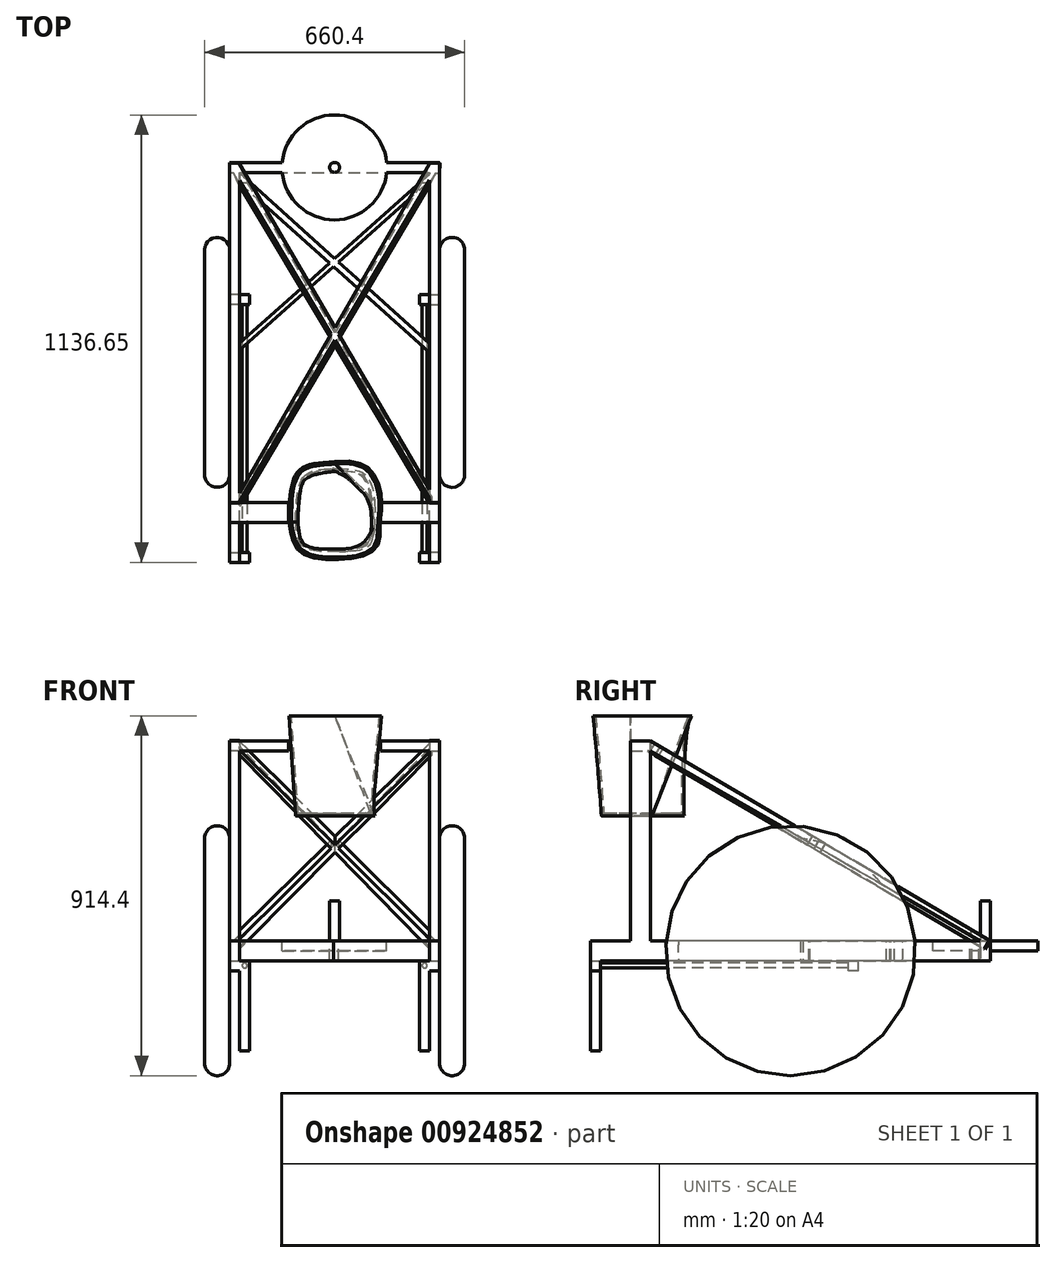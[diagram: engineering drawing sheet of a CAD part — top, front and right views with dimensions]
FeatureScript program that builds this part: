
annotation { "Feature Type Name" : "Feature", "Feature Type Description" : "" }
export const myFeature = defineFeature(function(context is Context, id is Id, definition is map)
    precondition{}
    {
        {
            var Q0;
            Q0=qCreatedBy(makeId("Right.planeOp"),FACE);
            var sketch = newSketch(context, id + "F0", { "sketchPlane" : qUnion([Q0])});
            skCircle(sketch, "E0", {"center": v(0, 317.5) * mm, "radius": 317.5 * mm});
            skSolve(sketch);
        }
        {
            var Q0;
            Q0=makeQuery(id+"F0.imprint","IMPRINT",FACE,{"disambiguationData":[TD([[makeQuery(id+"F0.imprint","IMPRINT",EDGE,{"derivedFrom":sQuery(id+"F0.wireOp",EDGE,"E0")}),1.0]])]});
            extrude(context, id + "F1", {"entities" : qUnion([Q0]), "depth" : 330.2 * mm, "offsetDistance" : 25.4 * mm, "hasSecondDirection" : true, "secondDirectionOppositeDirection" : false, "secondDirectionDepth" : 266.7 * mm});
        }
        {
            var Q0;
            Q0=makeQuery(id+"FX83OG7cxAnBelo_1.opExtrude","CAP_EDGE",EDGE,{"disambiguationData":[OSD([sQuery(id+"F0.wireOp",EDGE,"E0")])],"isStart":false});
            var Q1;
            Q1=makeQuery(id+"FX83OG7cxAnBelo_1.opExtrude","CAP_EDGE",EDGE,{"disambiguationData":[OSD([sQuery(id+"F0.wireOp",EDGE,"E0")])],"isStart":true});
            var Q2;
            Q2=makeQuery(id+"F1.opExtrude","CAP_EDGE",EDGE,{"disambiguationData":[OSD([sQuery(id+"F0.wireOp",EDGE,"E0")])],"isStart":true});
            var Q3;
            Q3=makeQuery(id+"F1.opExtrude","SWEPT_FACE",FACE,{"disambiguationData":[OSD([sQuery(id+"F0.wireOp",EDGE,"E0")])]});
            fillet(context, id + "F2", {"entities" : qUnion([Q0, Q1, Q2, Q3]), "radius" : 31.75 * mm, "tangentPropagation" : true, "allowEdgeOverflow" : false});
        }
        {
            var Q0;
            Q0=qCreatedBy(makeId("Top.planeOp"),FACE);
            cPlane(context, id + "F3", {"entities" : qUnion([Q0]), "cplaneType" : CPlaneType.OFFSET, "offset" : 317.5 * mm, "width" : 152.4 * mm, "height" : 152.4 * mm});
        }
        {
            var Q0;
            Q0=qCreatedBy(id+"F3.planeOp",FACE);
            var sketch = newSketch(context, id + "F4", { "sketchPlane" : qUnion([Q0])});
            skLineSegment(sketch, "E1.bottom", {"start": v(266.7, 508) * mm, "end": v(241.3, 508) * mm});
            skLineSegment(sketch, "E1.top", {"start": v(266.7, -508) * mm, "end": v(241.3, -508) * mm});
            skLineSegment(sketch, "E1.left", {"start": v(266.7, 508) * mm, "end": v(266.7, -508) * mm});
            skLineSegment(sketch, "E1.right", {"start": v(241.3, 508) * mm, "end": v(241.3, -508) * mm});
            skSolve(sketch);
        }
        {
            var Q0;
            Q0=makeQuery(id+"F4.imprint","IMPRINT",FACE,{"disambiguationData":[TD([[makeQuery(id+"F4.imprint","IMPRINT",EDGE,{"derivedFrom":sQuery(id+"F4.wireOp",EDGE,"E1.bottom")}),1.0]])]});
            extrude(context, id + "F5", {"entities" : qUnion([Q0]), "operationType" : NewBodyOperationType.ADD, "depth" : 25.4 * mm, "offsetDistance" : 25.4 * mm, "hasSecondDirection" : true, "secondDirectionOppositeDirection" : true, "secondDirectionDepth" : 25.4 * mm});
        }
        {
            var Q0;
            Q0=makeQuery(id+"F5.opExtrude","CAP_FACE",FACE,{"disambiguationData":[OSD([sQuery(id+"F4.wireOp",EDGE,"E1.bottom"),sQuery(id+"F4.wireOp",EDGE,"E1.top"),sQuery(id+"F4.wireOp",EDGE,"E1.left"),sQuery(id+"F4.wireOp",EDGE,"E1.right")])],"isStart":false});
            var sketch = newSketch(context, id + "F6", { "sketchPlane" : qUnion([Q0])});
            skLineSegment(sketch, "E2.bottom", {"start": v(266.7, -406.4) * mm, "end": v(241.3, -406.4) * mm});
            skLineSegment(sketch, "E2.top", {"start": v(266.7, -355.6) * mm, "end": v(241.3, -355.6) * mm});
            skLineSegment(sketch, "E2.left", {"start": v(266.7, -406.4) * mm, "end": v(266.7, -355.6) * mm});
            skLineSegment(sketch, "E2.right", {"start": v(241.3, -406.4) * mm, "end": v(241.3, -355.6) * mm});
            skSolve(sketch);
        }
        {
            var Q0;
            Q0=qSketchRegion(id+"F6",true);
            extrude(context, id + "F7", {"entities" : qUnion([Q0]), "operationType" : NewBodyOperationType.ADD, "depth" : 508 * mm, "offsetDistance" : 25.4 * mm});
        }
        {
            var Q0;
            Q0=makeQuery(id+"F5.opExtrude","CAP_FACE",FACE,{"disambiguationData":[OSD([sQuery(id+"F4.wireOp",EDGE,"E1.bottom"),sQuery(id+"F4.wireOp",EDGE,"E1.top"),sQuery(id+"F4.wireOp",EDGE,"E1.left"),sQuery(id+"F4.wireOp",EDGE,"E1.right")])],"isStart":true});
            var sketch = newSketch(context, id + "F8", { "sketchPlane" : qUnion([Q0])});
            skLineSegment(sketch, "E3.bottom", {"start": v(266.7, 508) * mm, "end": v(241.3, 508) * mm});
            skLineSegment(sketch, "E3.top", {"start": v(266.7, 482.6) * mm, "end": v(241.3, 482.6) * mm});
            skLineSegment(sketch, "E3.left", {"start": v(266.7, 508) * mm, "end": v(266.7, 482.6) * mm});
            skLineSegment(sketch, "E3.right", {"start": v(241.3, 508) * mm, "end": v(241.3, 482.6) * mm});
            skLineSegment(sketch, "E4.bottom", {"start": v(241.3, -172.43) * mm, "end": v(266.7, -172.43) * mm});
            skLineSegment(sketch, "E4.top", {"start": v(241.3, -147.03) * mm, "end": v(266.7, -147.03) * mm});
            skLineSegment(sketch, "E4.left", {"start": v(241.3, -172.43) * mm, "end": v(241.3, -147.03) * mm});
            skLineSegment(sketch, "E4.right", {"start": v(266.7, -172.43) * mm, "end": v(266.7, -147.03) * mm});
            skSolve(sketch);
        }
        {
            var Q0;
            Q0=qSketchRegion(id+"F8",true);
            extrude(context, id + "F9", {"entities" : qUnion([Q0]), "operationType" : NewBodyOperationType.ADD, "depth" : 25.4 * mm, "offsetDistance" : 25.4 * mm});
        }
        {
            var Q0;
            Q0=makeQuery(id+"F9.boolean.opBoolean","MERGE",FACE,{"derivedFrom":[makeQuery(id+"F7.boolean.opBoolean","MERGE",FACE,{"derivedFrom":[makeQuery(id+"F5.opExtrude","SWEPT_FACE",FACE,{"disambiguationData":[OSD([sQuery(id+"F4.wireOp",EDGE,"E1.right")])]}),makeQuery(id+"F7.opExtrude","SWEPT_FACE",FACE,{"disambiguationData":[OSD([sQuery(id+"F6.wireOp",EDGE,"E2.right")])]})]}),makeQuery(id+"F9.opExtrude","SWEPT_FACE",FACE,{"disambiguationData":[OSD([sQuery(id+"F8.wireOp",EDGE,"E3.right")])]}),makeQuery(id+"F9.opExtrude","SWEPT_FACE",FACE,{"disambiguationData":[OSD([sQuery(id+"F8.wireOp",EDGE,"2GlEI7fU-vQDi-rjw4-ohAJ-rqm9R4m0vmAV.right")])]})]});
            var sketch = newSketch(context, id + "F10", { "sketchPlane" : qUnion([Q0])});
            skLineSegment(sketch, "E5.bottom", {"start": v(508, 266.7) * mm, "end": v(482.6, 266.7) * mm});
            skLineSegment(sketch, "E5.top", {"start": v(508, 292.1) * mm, "end": v(482.6, 292.1) * mm});
            skLineSegment(sketch, "E5.left", {"start": v(508, 266.7) * mm, "end": v(508, 292.1) * mm});
            skLineSegment(sketch, "E5.right", {"start": v(482.6, 266.7) * mm, "end": v(482.6, 292.1) * mm});
            skLineSegment(sketch, "E6.bottom", {"start": v(-172.43, 266.7) * mm, "end": v(-147.03, 266.7) * mm});
            skLineSegment(sketch, "E6.top", {"start": v(-172.43, 292.1) * mm, "end": v(-147.03, 292.1) * mm});
            skLineSegment(sketch, "E6.left", {"start": v(-172.43, 266.7) * mm, "end": v(-172.43, 292.1) * mm});
            skLineSegment(sketch, "E6.right", {"start": v(-147.03, 266.7) * mm, "end": v(-147.03, 292.1) * mm});
            skSolve(sketch);
        }
        {
            var Q0;
            Q0=qSketchRegion(id+"F10",true);
            extrude(context, id + "F11", {"entities" : qUnion([Q0]), "operationType" : NewBodyOperationType.ADD, "depth" : 25.4 * mm, "offsetDistance" : 25.4 * mm});
        }
        {
            var Q0;
            Q0=makeQuery(id+"F11.boolean.opBoolean","MERGE",FACE,{"derivedFrom":[makeQuery(id+"F9.opExtrude","SWEPT_FACE",FACE,{"disambiguationData":[OSD([sQuery(id+"F8.wireOp",EDGE,"E3.top")])]}),makeQuery(id+"F11.opExtrude","SWEPT_FACE",FACE,{"disambiguationData":[OSD([sQuery(id+"F10.wireOp",EDGE,"E5.right")])]})]});
            var sketch = newSketch(context, id + "F12", { "sketchPlane" : qUnion([Q0])});
            skCircle(sketch, "E7", {"center": v(-228.6, 279.75) * mm, "radius": 6.35 * mm});
            skSolve(sketch);
        }
        {
            var Q0;
            Q0=qSketchRegion(id+"F12",true);
            extrude(context, id + "F13", {"entities" : qUnion([Q0]), "operationType" : NewBodyOperationType.ADD, "depth" : 635 * mm, "offsetDistance" : 25.4 * mm});
        }
        {
            var Q0;
            Q0=makeQuery(id+"F9.boolean.opBoolean","MERGE",FACE,{"derivedFrom":[makeQuery(id+"F7.boolean.opBoolean","MERGE",FACE,{"derivedFrom":[makeQuery(id+"F5.opExtrude","SWEPT_FACE",FACE,{"disambiguationData":[OSD([sQuery(id+"F4.wireOp",EDGE,"E1.right")])]}),makeQuery(id+"F7.opExtrude","SWEPT_FACE",FACE,{"disambiguationData":[OSD([sQuery(id+"F6.wireOp",EDGE,"E2.right")])]})]}),makeQuery(id+"F9.opExtrude","SWEPT_FACE",FACE,{"disambiguationData":[OSD([sQuery(id+"F8.wireOp",EDGE,"E3.right")])]}),makeQuery(id+"F9.opExtrude","SWEPT_FACE",FACE,{"disambiguationData":[OSD([sQuery(id+"F8.wireOp",EDGE,"2GlEI7fU-vQDi-rjw4-ohAJ-rqm9R4m0vmAV.right")])]})]});
            var sketch = newSketch(context, id + "F14", { "sketchPlane" : qUnion([Q0])});
            skLineSegment(sketch, "E8.bottom", {"start": v(406.4, 850.9) * mm, "end": v(355.6, 850.9) * mm});
            skLineSegment(sketch, "E8.top", {"start": v(406.4, 825.5) * mm, "end": v(355.6, 825.5) * mm});
            skLineSegment(sketch, "E8.left", {"start": v(406.4, 850.9) * mm, "end": v(406.4, 825.5) * mm});
            skLineSegment(sketch, "E8.right", {"start": v(355.6, 850.9) * mm, "end": v(355.6, 825.5) * mm});
            skSolve(sketch);
        }
        {
            var Q0;
            Q0=qSketchRegion(id+"F14",true);
            extrude(context, id + "F15", {"entities" : qUnion([Q0]), "operationType" : NewBodyOperationType.ADD, "depth" : 124.28 * mm, "offsetDistance" : 25.4 * mm});
        }
        {
            var Q0;
            {var subQ0=sQuery(id+"F0.wireOp",EDGE,"E0");var subQ1=sQuery(id+"F4.wireOp",EDGE,"E1.left");Q0=makeQuery(id+"F5.boolean.opBoolean","SPLIT",FACE,{"disambiguationData":[TD([makeQuery(id+"F5.opExtrude","CAP_FACE",FACE,{"disambiguationData":[OSD([sQuery(id+"F4.wireOp",EDGE,"E1.bottom"),sQuery(id+"F4.wireOp",EDGE,"E1.top"),subQ1,sQuery(id+"F4.wireOp",EDGE,"E1.right")])],"isStart":false})])],"derivedFrom":makeQuery(id+"F1.opExtrude","CAP_FACE",FACE,{"disambiguationData":[OSD([subQ0])],"isStart":true})});}
            cPlane(context, id + "F16", {"entities" : qUnion([Q0]), "cplaneType" : CPlaneType.OFFSET, "offset" : 0 * mm, "width" : 152.4 * mm, "height" : 152.4 * mm});
        }
        {
            var Q0;
            Q0=qCreatedBy(id+"F16.planeOp",FACE);
            var sketch = newSketch(context, id + "F17", { "sketchPlane" : qUnion([Q0])});
            skLineSegment(sketch, "E9", {"start": v(-507.39, 342.38) * mm, "end": v(356.93, 851.2) * mm});
            skLineSegment(sketch, "E10", {"start": v(356.93, 851.2) * mm, "end": v(356.93, 825.8) * mm});
            skLineSegment(sketch, "E11", {"start": v(356.93, 825.8) * mm, "end": v(-481.99, 342.38) * mm});
            skLineSegment(sketch, "E12", {"start": v(-481.99, 342.38) * mm, "end": v(-507.39, 342.38) * mm});
            skSolve(sketch);
        }
        {
            var Q0;
            Q0=qSketchRegion(id+"F17",true);
            extrude(context, id + "F18", {"entities" : qUnion([Q0]), "operationType" : NewBodyOperationType.ADD, "depth" : 25.4 * mm, "offsetDistance" : 25.4 * mm});
        }
        {
            var Q0;
            Q0=makeQuery(id+"F1.opExtrude","SWEPT_BODY",BODY,{"disambiguationData":[OSD([sQuery(id+"F0.wireOp",EDGE,"E0")])]});
            var Q1;
            Q1=qCreatedBy(makeId("Right.planeOp"),FACE);
            mirror(context, id + "F19", {"operationType" : NewBodyOperationType.ADD, "entities" : qUnion([Q0]), "mirrorPlane" : qUnion([Q1])});
        }
        {
            var Q0;
            {var subQ0=sQuery(id+"F0.wireOp",EDGE,"E0");var subQ6=sQuery(id+"F17.wireOp",EDGE,"E9");Q0=makeQuery(id+"F18.boolean.opBoolean","SPLIT",FACE,{"disambiguationData":[TD([makeQuery(id+"F1.opExtrude","CAP_FACE",FACE,{"disambiguationData":[OSD([subQ0])],"isStart":true})])],"derivedFrom":makeQuery(id+"F18.opExtrude","SWEPT_FACE",FACE,{"disambiguationData":[OSD([subQ6])]})});}
            cPlane(context, id + "F20", {"entities" : qUnion([Q0]), "cplaneType" : CPlaneType.OFFSET, "offset" : 0 * mm, "oppositeDirection" : true, "width" : 152.4 * mm, "height" : 152.4 * mm});
        }
        {
            var Q0;
            Q0=qCreatedBy(id+"F20.planeOp",FACE);
            var sketch = newSketch(context, id + "F21", { "sketchPlane" : qUnion([Q0])});
            skLineSegment(sketch, "E13", {"start": v(-267.5, 260.99) * mm, "end": v(245.57, -734.84) * mm});
            skLineSegment(sketch, "E14", {"start": v(245.57, -734.84) * mm, "end": v(245.57, -709.44) * mm});
            skLineSegment(sketch, "E15", {"start": v(245.57, -709.44) * mm, "end": v(-242.1, 260.98) * mm});
            skLineSegment(sketch, "E16", {"start": v(-242.1, 260.98) * mm, "end": v(-267.5, 260.99) * mm});
            skSolve(sketch);
        }
        {
            var Q0;
            Q0=qSketchRegion(id+"F21",true);
            extrude(context, id + "F22", {"entities" : qUnion([Q0]), "operationType" : NewBodyOperationType.ADD, "oppositeDirection" : true, "depth" : 25.4 * mm, "offsetDistance" : 25.4 * mm});
        }
        {
            var Q0;
            Q0=qCreatedBy(id+"F20.planeOp",FACE);
            var sketch = newSketch(context, id + "F23", { "sketchPlane" : qUnion([Q0])});
            skLineSegment(sketch, "E17", {"start": v(-242.02, -737.2) * mm, "end": v(267.33, 262.61) * mm});
            skLineSegment(sketch, "E18", {"start": v(267.33, 262.61) * mm, "end": v(241.93, 262.61) * mm});
            skLineSegment(sketch, "E19", {"start": v(-242.02, -737.2) * mm, "end": v(-242.02, -711.8) * mm});
            skLineSegment(sketch, "E20", {"start": v(241.93, 262.61) * mm, "end": v(-242.02, -711.8) * mm});
            skSolve(sketch);
        }
        {
            var Q0;
            Q0=qSketchRegion(id+"F23",true);
            extrude(context, id + "F24", {"entities" : qUnion([Q0]), "operationType" : NewBodyOperationType.ADD, "oppositeDirection" : true, "depth" : 25.4 * mm, "offsetDistance" : 25.4 * mm});
        }
        {
            var Q0;
            {var subQ0=sQuery(id+"F17.wireOp",EDGE,"E11");var subQ1=sQuery(id+"F17.wireOp",EDGE,"E9");var subQ6=sQuery(id+"F4.wireOp",EDGE,"E1.right");var subQ9=sQuery(id+"F4.wireOp",EDGE,"E1.bottom");var subQ10=sQuery(id+"F17.wireOp",EDGE,"E12");Q0=makeQuery(id+"F22.boolean.opBoolean","SPLIT",FACE,{"disambiguationData":[TD([makeQuery(id+"F5.opExtrude","SWEPT_FACE",FACE,{"disambiguationData":[OSD([subQ9])]})])],"derivedFrom":makeQuery(id+"F18.boolean.opBoolean","MERGE",FACE,{"derivedFrom":[makeQuery(id+"F9.boolean.opBoolean","MERGE",FACE,{"derivedFrom":[makeQuery(id+"F7.boolean.opBoolean","MERGE",FACE,{"derivedFrom":[makeQuery(id+"F5.opExtrude","SWEPT_FACE",FACE,{"disambiguationData":[OSD([subQ6])]}),makeQuery(id+"F7.opExtrude","SWEPT_FACE",FACE,{"disambiguationData":[OSD([sQuery(id+"F6.wireOp",EDGE,"E2.right")])]})]}),makeQuery(id+"F9.opExtrude","SWEPT_FACE",FACE,{"disambiguationData":[OSD([sQuery(id+"F8.wireOp",EDGE,"E3.right")])]}),makeQuery(id+"F9.opExtrude","SWEPT_FACE",FACE,{"disambiguationData":[OSD([sQuery(id+"F8.wireOp",EDGE,"E4.left")])]})]}),makeQuery(id+"F18.opExtrude","CAP_FACE",FACE,{"disambiguationData":[OSD([subQ1,sQuery(id+"F17.wireOp",EDGE,"E10"),subQ0,subQ10])],"isStart":false})]})});}
            var sketch = newSketch(context, id + "F25", { "sketchPlane" : qUnion([Q0])});
            skLineSegment(sketch, "E21.bottom", {"start": v(-508, 342.9) * mm, "end": v(-482.6, 342.9) * mm});
            skLineSegment(sketch, "E21.top", {"start": v(-508, 292.1) * mm, "end": v(-482.6, 292.1) * mm});
            skLineSegment(sketch, "E21.left", {"start": v(-508, 342.9) * mm, "end": v(-508, 292.1) * mm});
            skLineSegment(sketch, "E21.right", {"start": v(-482.6, 342.9) * mm, "end": v(-482.6, 292.1) * mm});
            skSolve(sketch);
        }
        {
            var Q0;
            Q0=qSketchRegion(id+"F25",true);
            extrude(context, id + "F26", {"entities" : qUnion([Q0]), "operationType" : NewBodyOperationType.ADD, "depth" : 482.6 * mm, "offsetDistance" : 25.4 * mm});
        }
        {
            var Q0;
            {var subQ0=sQuery(id+"F4.wireOp",EDGE,"E1.left");var subQ2=sQuery(id+"F4.wireOp",EDGE,"E1.bottom");var subQ3=makeQuery(id+"F5.opExtrude","SWEPT_FACE",FACE,{"disambiguationData":[OSD([subQ2])]});var subQ4=sQuery(id+"F0.wireOp",EDGE,"E0");var subQ6=makeQuery(id+"F1.opExtrude","CAP_FACE",FACE,{"disambiguationData":[OSD([subQ4])],"isStart":true});var subQ8=sQuery(id+"F4.wireOp",EDGE,"E1.right");var subQ11=makeQuery(id+"F18.boolean.opBoolean","SPLIT",FACE,{"disambiguationData":[TD([subQ3])],"derivedFrom":makeQuery(id+"F7.boolean.opBoolean","SPLIT",FACE,{"disambiguationData":[TD([subQ6])],"derivedFrom":makeQuery(id+"F5.opExtrude","CAP_FACE",FACE,{"disambiguationData":[OSD([subQ2,sQuery(id+"F4.wireOp",EDGE,"E1.top"),subQ0,subQ8])],"isStart":false})})});Q0=makeQuery(id+"F26.boolean.opBoolean","MERGE",FACE,{"derivedFrom":[makeQuery(id+"F19.opPattern","COPY",FACE,{"derivedFrom":subQ11,"instanceName":"1"}),subQ11,makeQuery(id+"F26.opExtrude","SWEPT_FACE",FACE,{"disambiguationData":[OSD([sQuery(id+"F25.wireOp",EDGE,"E21.bottom")])]})]});}
            var sketch = newSketch(context, id + "F27", { "sketchPlane" : qUnion([Q0])});
            skCircle(sketch, "E22", {"center": v(-0.43, 495.3) * mm, "radius": 133.35 * mm});
            skPoint(sketch, "E22.centerSnap0", {"position": v(-0.43, 482.6) * mm});
            skSolve(sketch);
        }
        {
            var Q0;
            {var subQ0=sQuery(id+"F27.wireOp",EDGE,"E22");var subQ1=makeQuery(id+"F26.opExtrude","SWEPT_EDGE",EDGE,{"disambiguationData":[OSD([sQuery(id+"F4.wireOp",EDGE,"E1.right"),sQuery(id+"F25.wireOp",EDGE,"E21.bottom"),sQuery(id+"F25.wireOp",EDGE,"E21.right")])]});var subQ2=makeQuery(id+"F27.imprint","INTERSECT",VERTEX,{"disambiguationData":[OD(0.0)],"derivedFrom":[subQ1,subQ0]});Q0=makeQuery(id+"F27.imprint","IMPRINT",FACE,{"disambiguationData":[TD([[makeQuery(id+"F27.imprint","IMPRINT",EDGE,{"disambiguationData":[TD([[subQ2,-1.0]])],"derivedFrom":subQ0}),1.0]])]});}
            var Q1;
            {var subQ0=sQuery(id+"F27.wireOp",EDGE,"E22");var subQ1=sQuery(id+"F25.wireOp",EDGE,"E21.bottom");var subQ5=makeQuery(id+"F26.opExtrude","SWEPT_EDGE",EDGE,{"disambiguationData":[OSD([sQuery(id+"F4.wireOp",EDGE,"E1.right"),subQ1,sQuery(id+"F25.wireOp",EDGE,"E21.right")])]});var subQ6=makeQuery(id+"F27.imprint","INTERSECT",VERTEX,{"disambiguationData":[OD(0.0)],"derivedFrom":[subQ5,subQ0]});Q1=makeQuery(id+"F27.imprint","IMPRINT",FACE,{"disambiguationData":[TD([[makeQuery(id+"F27.imprint","IMPRINT",EDGE,{"disambiguationData":[TD([[subQ6,1.0]])],"derivedFrom":subQ0}),1.0]])]});}
            var Q2;
            {var subQ0=sQuery(id+"F27.wireOp",EDGE,"E22");var subQ1=makeQuery(id+"F5.opExtrude","CAP_EDGE",EDGE,{"disambiguationData":[OSD([sQuery(id+"F4.wireOp",EDGE,"E1.bottom")])],"isStart":false});var subQ2=makeQuery(id+"F26.boolean.opBoolean","MERGE",EDGE,{"derivedFrom":[subQ1,makeQuery(id+"F19.opPattern","COPY",EDGE,{"derivedFrom":subQ1,"instanceName":"1"}),makeQuery(id+"F26.opExtrude","SWEPT_EDGE",EDGE,{"disambiguationData":[OSD([sQuery(id+"F25.wireOp",EDGE,"E21.bottom"),sQuery(id+"F25.wireOp",EDGE,"E21.left")])]})]});var subQ3=makeQuery(id+"F27.imprint","INTERSECT",VERTEX,{"disambiguationData":[OD(0.0)],"derivedFrom":[subQ2,subQ0]});Q2=makeQuery(id+"F27.imprint","IMPRINT",FACE,{"disambiguationData":[TD([[makeQuery(id+"F27.imprint","IMPRINT",EDGE,{"disambiguationData":[TD([[subQ3,1.0]])],"derivedFrom":subQ0}),1.0]])]});}
            extrude(context, id + "F28", {"entities" : qUnion([Q0, Q1, Q2]), "operationType" : NewBodyOperationType.ADD, "oppositeDirection" : true, "depth" : 25.4 * mm, "offsetDistance" : 25.4 * mm});
        }
        {
            var Q0;
            {var subQ0=sQuery(id+"F4.wireOp",EDGE,"E1.left");var subQ2=sQuery(id+"F4.wireOp",EDGE,"E1.bottom");var subQ3=makeQuery(id+"F5.opExtrude","SWEPT_FACE",FACE,{"disambiguationData":[OSD([subQ2])]});var subQ4=sQuery(id+"F0.wireOp",EDGE,"E0");var subQ6=makeQuery(id+"F1.opExtrude","CAP_FACE",FACE,{"disambiguationData":[OSD([subQ4])],"isStart":true});var subQ8=sQuery(id+"F4.wireOp",EDGE,"E1.right");var subQ11=makeQuery(id+"F18.boolean.opBoolean","SPLIT",FACE,{"disambiguationData":[TD([subQ3])],"derivedFrom":makeQuery(id+"F7.boolean.opBoolean","SPLIT",FACE,{"disambiguationData":[TD([subQ6])],"derivedFrom":makeQuery(id+"F5.opExtrude","CAP_FACE",FACE,{"disambiguationData":[OSD([subQ2,sQuery(id+"F4.wireOp",EDGE,"E1.top"),subQ0,subQ8])],"isStart":false})})});Q0=makeQuery(id+"F28.boolean.opBoolean","MERGE",FACE,{"derivedFrom":[makeQuery(id+"F26.boolean.opBoolean","MERGE",FACE,{"derivedFrom":[makeQuery(id+"F19.opPattern","COPY",FACE,{"derivedFrom":subQ11,"instanceName":"1"}),subQ11,makeQuery(id+"F26.opExtrude","SWEPT_FACE",FACE,{"disambiguationData":[OSD([sQuery(id+"F25.wireOp",EDGE,"E21.bottom")])]})]}),makeQuery(id+"F28.opExtrude","CAP_FACE",FACE,{"disambiguationData":[OSD([sQuery(id+"F27.wireOp",EDGE,"E22")])],"isStart":true})]});}
            var sketch = newSketch(context, id + "F29", { "sketchPlane" : qUnion([Q0])});
            skCircle(sketch, "E23", {"center": v(0, 495.3) * mm, "radius": 12.7 * mm});
            skSolve(sketch);
        }
        {
            var Q0;
            Q0=makeQuery(id+"F29.imprint","IMPRINT",FACE,{"disambiguationData":[TD([[makeQuery(id+"F29.imprint","IMPRINT",EDGE,{"derivedFrom":sQuery(id+"F29.wireOp",EDGE,"E23")}),1.0]])]});
            extrude(context, id + "F30", {"entities" : qUnion([Q0]), "operationType" : NewBodyOperationType.ADD, "depth" : 101.6 * mm, "offsetDistance" : 25.4 * mm});
        }
        {
            var Q0;
            {var subQ0=sQuery(id+"F4.wireOp",EDGE,"E1.left");var subQ2=sQuery(id+"F4.wireOp",EDGE,"E1.bottom");var subQ3=makeQuery(id+"F5.opExtrude","SWEPT_FACE",FACE,{"disambiguationData":[OSD([subQ2])]});var subQ4=sQuery(id+"F0.wireOp",EDGE,"E0");var subQ6=makeQuery(id+"F1.opExtrude","CAP_FACE",FACE,{"disambiguationData":[OSD([subQ4])],"isStart":true});var subQ8=sQuery(id+"F4.wireOp",EDGE,"E1.right");var subQ11=makeQuery(id+"F18.boolean.opBoolean","SPLIT",FACE,{"disambiguationData":[TD([subQ3])],"derivedFrom":makeQuery(id+"F7.boolean.opBoolean","SPLIT",FACE,{"disambiguationData":[TD([subQ6])],"derivedFrom":makeQuery(id+"F5.opExtrude","CAP_FACE",FACE,{"disambiguationData":[OSD([subQ2,sQuery(id+"F4.wireOp",EDGE,"E1.top"),subQ0,subQ8])],"isStart":false})})});Q0=makeQuery(id+"F28.boolean.opBoolean","MERGE",FACE,{"derivedFrom":[makeQuery(id+"F26.boolean.opBoolean","MERGE",FACE,{"derivedFrom":[makeQuery(id+"F19.opPattern","COPY",FACE,{"derivedFrom":subQ11,"instanceName":"1"}),subQ11,makeQuery(id+"F26.opExtrude","SWEPT_FACE",FACE,{"disambiguationData":[OSD([sQuery(id+"F25.wireOp",EDGE,"E21.bottom")])]})]}),makeQuery(id+"F28.opExtrude","CAP_FACE",FACE,{"disambiguationData":[OSD([sQuery(id+"F27.wireOp",EDGE,"E22")])],"isStart":true})]});}
            var sketch = newSketch(context, id + "F31", { "sketchPlane" : qUnion([Q0])});
            skLineSegment(sketch, "E24", {"start": v(-267.03, 26) * mm, "end": v(241.3, 478.6) * mm});
            skLineSegment(sketch, "E25", {"start": v(241.3, 478.6) * mm, "end": v(242.1, 461.39) * mm});
            skLineSegment(sketch, "E26", {"start": v(242.1, 461.39) * mm, "end": v(-247.23, 26) * mm});
            skLineSegment(sketch, "E27", {"start": v(-247.23, 26) * mm, "end": v(-267.03, 26) * mm});
            skLineSegment(sketch, "E28", {"start": v(266.7, 24.54) * mm, "end": v(-241.23, 480.61) * mm});
            skLineSegment(sketch, "E29", {"start": v(-241.23, 480.61) * mm, "end": v(-241.23, 455.21) * mm});
            skLineSegment(sketch, "E30", {"start": v(-241.23, 455.21) * mm, "end": v(241.47, 25.19) * mm});
            skLineSegment(sketch, "E31", {"start": v(241.3, 25.2) * mm, "end": v(266.7, 24.54) * mm});
            skSolve(sketch);
        }
        {
            var Q0;
            Q0=qSketchRegion(id+"F31",true);
            extrude(context, id + "F32", {"entities" : qUnion([Q0]), "operationType" : NewBodyOperationType.ADD, "oppositeDirection" : true, "depth" : 50.8 * mm, "offsetDistance" : 25.4 * mm});
        }
        {
            var Q0;
            Q0=makeQuery(id+"F19.opPattern","COPY",FACE,{"derivedFrom":makeQuery(id+"F11.boolean.opBoolean","MERGE",FACE,{"derivedFrom":[makeQuery(id+"F9.opExtrude","CAP_FACE",FACE,{"disambiguationData":[OSD([sQuery(id+"F8.wireOp",EDGE,"E3.bottom"),sQuery(id+"F8.wireOp",EDGE,"E3.top"),sQuery(id+"F8.wireOp",EDGE,"E3.left"),sQuery(id+"F8.wireOp",EDGE,"E3.right")])],"isStart":false}),makeQuery(id+"F11.opExtrude","SWEPT_FACE",FACE,{"disambiguationData":[OSD([sQuery(id+"F10.wireOp",EDGE,"E5.bottom")])]})]}),"instanceName":"1"});
            var sketch = newSketch(context, id + "F33", { "sketchPlane" : qUnion([Q0])});
            skLineSegment(sketch, "E32.bottom", {"start": v(-215.9, 508) * mm, "end": v(-241.3, 508) * mm});
            skLineSegment(sketch, "E32.top", {"start": v(-215.9, 482.6) * mm, "end": v(-241.3, 482.6) * mm});
            skLineSegment(sketch, "E32.left", {"start": v(-215.9, 508) * mm, "end": v(-215.9, 482.6) * mm});
            skLineSegment(sketch, "E32.right", {"start": v(-241.3, 508) * mm, "end": v(-241.3, 482.6) * mm});
            skSolve(sketch);
        }
        {
            var Q0;
            Q0=qSketchRegion(id+"F33",true);
            extrude(context, id + "F34", {"entities" : qUnion([Q0]), "operationType" : NewBodyOperationType.ADD, "depth" : 203.2 * mm, "offsetDistance" : 25.4 * mm});
        }
        {
            var Q0;
            Q0=makeQuery(id+"F11.boolean.opBoolean","MERGE",FACE,{"derivedFrom":[makeQuery(id+"F9.opExtrude","CAP_FACE",FACE,{"disambiguationData":[OSD([sQuery(id+"F8.wireOp",EDGE,"E3.bottom"),sQuery(id+"F8.wireOp",EDGE,"E3.top"),sQuery(id+"F8.wireOp",EDGE,"E3.left"),sQuery(id+"F8.wireOp",EDGE,"E3.right")])],"isStart":false}),makeQuery(id+"F11.opExtrude","SWEPT_FACE",FACE,{"disambiguationData":[OSD([sQuery(id+"F10.wireOp",EDGE,"E5.bottom")])]})]});
            var sketch = newSketch(context, id + "F35", { "sketchPlane" : qUnion([Q0])});
            skLineSegment(sketch, "E33.bottom", {"start": v(215.9, 508) * mm, "end": v(241.3, 508) * mm});
            skLineSegment(sketch, "E33.top", {"start": v(215.9, 482.6) * mm, "end": v(241.3, 482.6) * mm});
            skLineSegment(sketch, "E33.left", {"start": v(215.9, 508) * mm, "end": v(215.9, 482.6) * mm});
            skLineSegment(sketch, "E33.right", {"start": v(241.3, 508) * mm, "end": v(241.3, 482.6) * mm});
            skSolve(sketch);
        }
        {
            var Q0;
            Q0=qSketchRegion(id+"F35",true);
            extrude(context, id + "F36", {"entities" : qUnion([Q0]), "operationType" : NewBodyOperationType.ADD, "depth" : 203.2 * mm, "offsetDistance" : 25.4 * mm});
        }
        {
            var Q0;
            Q0=qCreatedBy(makeId("Top.planeOp"),FACE);
            cPlane(context, id + "F37", {"entities" : qUnion([Q0]), "cplaneType" : CPlaneType.OFFSET, "offset" : 914.4 * mm, "width" : 152.4 * mm, "height" : 152.4 * mm});
        }
        {
            var Q0;
            Q0=qCreatedBy(id+"F37.planeOp",FACE);
            var sketch = newSketch(context, id + "F38", { "sketchPlane" : qUnion([Q0])});
            skFitSpline(sketch, "E34", {"points": [v(-116.29, -406.52) * mm, v(-114.53, -353.7) * mm, v(-93.4, -278) * mm, v(0, -251.6) * mm], "startDerivative": vector(5.7, 179.42) * mm, "endDerivative": vector(346.1, 27.63) * mm});
            skFitSpline(sketch, "E35", {"points": [v(0, -251.6) * mm, v(94.97, -278) * mm, v(119.62, -353.7) * mm, v(116.1, -406.52) * mm, v(103.78, -473.42) * mm, v(0, -501.59) * mm, v(-93.4, -476.94) * mm, v(-116.29, -406.52) * mm], "startDerivative": vector(965.92, 66.74) * mm, "endDerivative": vector(-120.36, 547.83) * mm});
            skSolve(sketch);
        }
        {
            var Q0;
            Q0=qCreatedBy(makeId("Top.planeOp"),FACE);
            cPlane(context, id + "F39", {"entities" : qUnion([Q0]), "cplaneType" : CPlaneType.OFFSET, "offset" : 660.4 * mm, "width" : 152.4 * mm, "height" : 152.4 * mm});
        }
        {
            var Q0;
            Q0=qCreatedBy(id+"F39.planeOp",FACE);
            var sketch = newSketch(context, id + "F40", { "sketchPlane" : qUnion([Q0])});
            skFitSpline(sketch, "E36", {"points": [v(-98.8, -406.39) * mm, v(-96.6, -350.68) * mm, v(-75.64, -287.24) * mm, v(0, -270.14) * mm, v(76.6, -284.48) * mm, v(101.42, -353.43) * mm, v(98.11, -433.97) * mm, v(82.67, -470.37) * mm, v(0, -480.85) * mm, v(-82.26, -465.96) * mm, v(-98.8, -406.39) * mm]});
            skSolve(sketch);
        }
        {
            var Q0;
            Q0=makeQuery(id+"F40.imprint","IMPRINT",FACE,{"disambiguationData":[TD([[makeQuery(id+"F40.imprint","IMPRINT",EDGE,{"derivedFrom":sQuery(id+"F40.wireOp",EDGE,"E36")}),-1.0]])]});
            var Q1;
            Q1=makeQuery(id+"F38.imprint","IMPRINT",FACE,{"disambiguationData":[TD([[makeQuery(id+"F38.imprint","IMPRINT",EDGE,{"derivedFrom":sQuery(id+"F38.wireOp",EDGE,"E34")}),-1.0]])]});
            loft(context, id + "F41", {"sheetProfilesArray" : [{ "sheetProfileEntities" : qUnion([Q0]) }, { "sheetProfileEntities" : qUnion([Q1]) }]});
        }
        {
            var Q0;
            Q0=makeQuery(id+"F41.opLoft","CAP_FACE",FACE,{"disambiguationData":[OSD([makeQuery(id+"F38.imprint","IMPRINT",FACE,{"disambiguationData":[TD([[makeQuery(id+"F38.imprint","IMPRINT",EDGE,{"derivedFrom":sQuery(id+"F38.wireOp",EDGE,"E34")}),-1.0]])]})])],"isStart":true});
            shell(context, id + "F42", {"entities" : qUnion([Q0]), "thickness" : 6.35 * mm});
        }
        {
            var Q0;
            Q0=qCreatedBy(id+"F39.planeOp",FACE);
            var sketch = newSketch(context, id + "F43", { "sketchPlane" : qUnion([Q0])});
            skFitSpline(sketch, "E37.0", {"points": [v(94.97, -352.2) * mm, v(94.66, -348.12) * mm, v(93.85, -340) * mm, v(91.96, -328.27) * mm, v(89.27, -317.27) * mm, v(85.68, -307.32) * mm, v(81.88, -300.15) * mm, v(78.34, -295.2) * mm, v(75.91, -292.45) * mm, v(73.84, -290.46) * mm, v(72.21, -289.07) * mm, v(70.5, -287.78) * mm, v(68.1, -286.17) * mm, v(64.84, -284.35) * mm, v(59.15, -281.85) * mm, v(51.14, -279.47) * mm, v(40.31, -277.64) * mm, v(28.53, -276.67) * mm, v(18.14, -276.4) * mm, v(9.62, -276.39) * mm, v(3.13, -276.45) * mm, v(-3.4, -276.54) * mm, v(-9.88, -276.66) * mm, v(-16.28, -276.86) * mm, v(-24.68, -277.26) * mm, v(-34.79, -278.1) * mm, v(-46.03, -279.88) * mm, v(-54.4, -282.18) * mm, v(-60.35, -284.57) * mm, v(-64.41, -286.65) * mm, v(-67.45, -288.64) * mm, v(-69.68, -290.4) * mm, v(-71.24, -291.8) * mm, v(-72.72, -293.3) * mm, v(-74.6, -295.44) * mm, v(-76.75, -298.4) * mm, v(-79.07, -302.37) * mm, v(-81.82, -308.16) * mm, v(-84.6, -316.2) * mm, v(-86.65, -324.94) * mm, v(-87.93, -332.13) * mm, v(-88.73, -337.55) * mm, v(-89.4, -342.96) * mm, v(-89.99, -348.3) * mm, v(-90.5, -353.5) * mm, v(-90.96, -358.52) * mm, v(-91.37, -363.4) * mm, v(-91.83, -369.72) * mm, v(-92.27, -377.42) * mm, v(-92.57, -386.58) * mm, v(-92.65, -395.95) * mm, v(-92.55, -402.5) * mm, v(-92.47, -405.91) * mm]});
            skFitSpline(sketch, "E37.1", {"points": [v(-92.47, -405.91) * mm, v(-92.38, -409.32) * mm, v(-92.14, -416.32) * mm, v(-91.28, -426.96) * mm, v(-89.67, -437.25) * mm, v(-87.52, -445.13) * mm, v(-85.25, -450.77) * mm, v(-83.59, -453.98) * mm, v(-82.1, -456.33) * mm, v(-80.92, -457.99) * mm, v(-79.66, -459.53) * mm, v(-78.33, -460.96) * mm, v(-76.9, -462.28) * mm, v(-74.83, -463.94) * mm, v(-71.95, -465.82) * mm, v(-68, -467.78) * mm, v(-63.58, -469.46) * mm, v(-58.7, -470.85) * mm, v(-51.68, -472.35) * mm, v(-41.97, -473.61) * mm, v(-31.33, -474.22) * mm, v(-22.41, -474.44) * mm, v(-15.57, -474.51) * mm, v(-9.75, -474.52) * mm, v(-5.06, -474.51) * mm, v(-1.52, -474.5) * mm, v(2.03, -474.5) * mm, v(6.76, -474.5) * mm, v(12.65, -474.49) * mm, v(19.63, -474.45) * mm, v(28.78, -474.33) * mm, v(39.82, -473.97) * mm, v(52.06, -473.03) * mm, v(61.1, -471.67) * mm, v(67.45, -470.17) * mm, v(71, -469.07) * mm, v(73.55, -468.09) * mm, v(75.32, -467.3) * mm, v(76.95, -466.47) * mm, v(78.4, -465.6) * mm, v(79.72, -464.7) * mm, v(81.32, -463.41) * mm, v(83.05, -461.67) * mm, v(84.82, -459.3) * mm, v(86.34, -456.6) * mm, v(87.65, -453.51) * mm, v(88.77, -450.05) * mm, v(89.71, -446.23) * mm, v(90.52, -442.06) * mm, v(91.1, -438.32) * mm, v(91.55, -435.18) * mm, v(91.87, -432.76) * mm, v(92.19, -430.28) * mm, v(92.6, -426.92) * mm, v(93.1, -422.6) * mm, v(93.67, -417.27) * mm, v(94.36, -409.97) * mm, v(95.08, -400.5) * mm, v(95.67, -388.75) * mm, v(95.9, -376.7) * mm, v(95.72, -364.47) * mm, v(95.28, -356.29) * mm, v(94.97, -352.2) * mm]});
            skSolve(sketch);
        }
        {
            var Q0;
            Q0=makeQuery(id+"F43.imprint","IMPRINT",FACE,{"disambiguationData":[TD([[makeQuery(id+"F43.imprint","IMPRINT",EDGE,{"derivedFrom":sQuery(id+"F43.wireOp",EDGE,"E37.0")}),1.0]])]});
            extrude(context, id + "F44", {"entities" : qUnion([Q0]), "operationType" : NewBodyOperationType.REMOVE, "depth" : 6.35 * mm, "offsetDistance" : 25.4 * mm});
        }
    });
